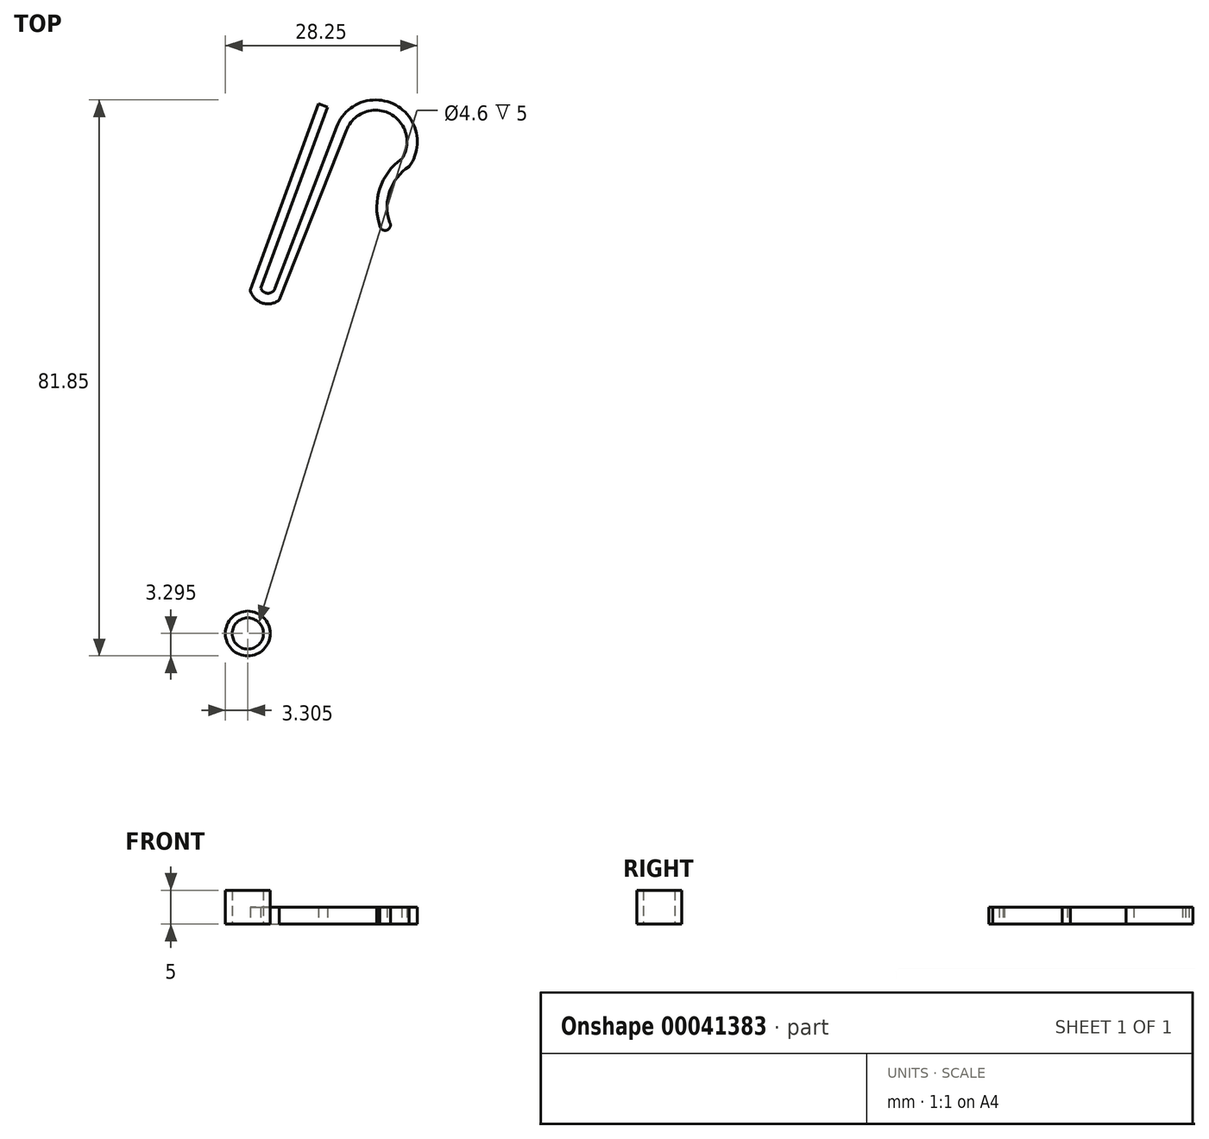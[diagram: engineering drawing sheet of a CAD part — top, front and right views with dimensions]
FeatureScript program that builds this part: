
annotation { "Feature Type Name" : "Feature", "Feature Type Description" : "" }
export const myFeature = defineFeature(function(context is Context, id is Id, definition is map)
    precondition{}
    {
        {
            var Q0;
            Q0=qCreatedBy(makeId("Top.planeOp"),FACE);
            var sketch = newSketch(context, id + "F0", { "sketchPlane" : qUnion([Q0])});
            skLineSegment(sketch, "E0", {"start": v(-39.45, -2.59) * mm, "end": v(-30.4, 21.18) * mm});
            skLineSegment(sketch, "E1", {"start": v(-24.36, 25.94) * mm, "end": v(-24.36, 23.62) * mm});
            skArc(sketch, "E2", {"start": v(-20.8, 16.45) * mm, "mid": v(-22.52, 23.1) * mm, "end": v(-28.96, 20.7) * mm});
            skLineSegment(sketch, "E3", {"start": v(-41.55, -2.59) * mm, "end": v(-31.74, 24.1) * mm});
            skLineSegment(sketch, "E4", {"start": v(-31.74, 24.1) * mm, "end": v(-33.05, 24.58) * mm});
            skLineSegment(sketch, "E5", {"start": v(-33.05, 24.58) * mm, "end": v(-43.11, -2.8) * mm});
            skArc(sketch, "E6.0", {"start": v(-43.11, -2.8) * mm, "mid": v(-41.39, -4.72) * mm, "end": v(-38.84, -4.3) * mm});
            skLineSegment(sketch, "E7", {"start": v(-38.84, -4.3) * mm, "end": v(-28.96, 20.7) * mm});
            skPoint(sketch, "E8.orphan", {"position": v(-28.51, 16.45) * mm});
            skPoint(sketch, "E9.orphan", {"position": v(-28.51, 21.84) * mm});
            skArc(sketch, "E10", {"start": v(-20.8, 16.45) * mm, "mid": v(-24.05, 12.1) * mm, "end": v(-24.05, 6.68) * mm});
            skArc(sketch, "E11.0", {"start": v(-19.72, 15.35) * mm, "mid": v(-22.56, 11.75) * mm, "end": v(-22.6, 7.16) * mm});
            skArc(sketch, "E11.1", {"start": v(-19.72, 15.35) * mm, "mid": v(-21.71, 24.4) * mm, "end": v(-30.4, 21.18) * mm});
            skArc(sketch, "E12", {"start": v(-41.55, -2.59) * mm, "mid": v(-40.5, -3.31) * mm, "end": v(-39.45, -2.59) * mm});
            skLineSegment(sketch, "E13", {"start": v(-31.03, 15.46) * mm, "end": v(-23.17, 13.96) * mm, "construction": true});
            skArc(sketch, "E14", {"start": v(-24.05, 6.68) * mm, "mid": v(-23.01, 5.98) * mm, "end": v(-22.6, 7.16) * mm});
            skSolve(sketch);
        }
        {
            var Q0;
            Q0 = qSketchRegion(id + "F0", true);
            extrude(context, id + "F1", {"entities" : qUnion([Q0]), "depth" : 2.5 * mm});
        }
        {
            var Q0;
            Q0=qCreatedBy(makeId("Top.planeOp"),FACE);
            var sketch = newSketch(context, id + "F2", { "sketchPlane" : qUnion([Q0])});
            skCircle(sketch, "E15.0", {"center": v(-43.47, -53.4) * mm, "radius": 3.3 * mm});
            skCircle(sketch, "E16", {"center": v(-43.47, -53.4) * mm, "radius": 2.3 * mm});
            skSolve(sketch);
        }
        {
            var Q0;
            Q0 = qSketchRegion(id + "F2", true);
            extrude(context, id + "F3", {"entities" : qUnion([Q0]), "depth" : 5 * mm});
        }
    });
